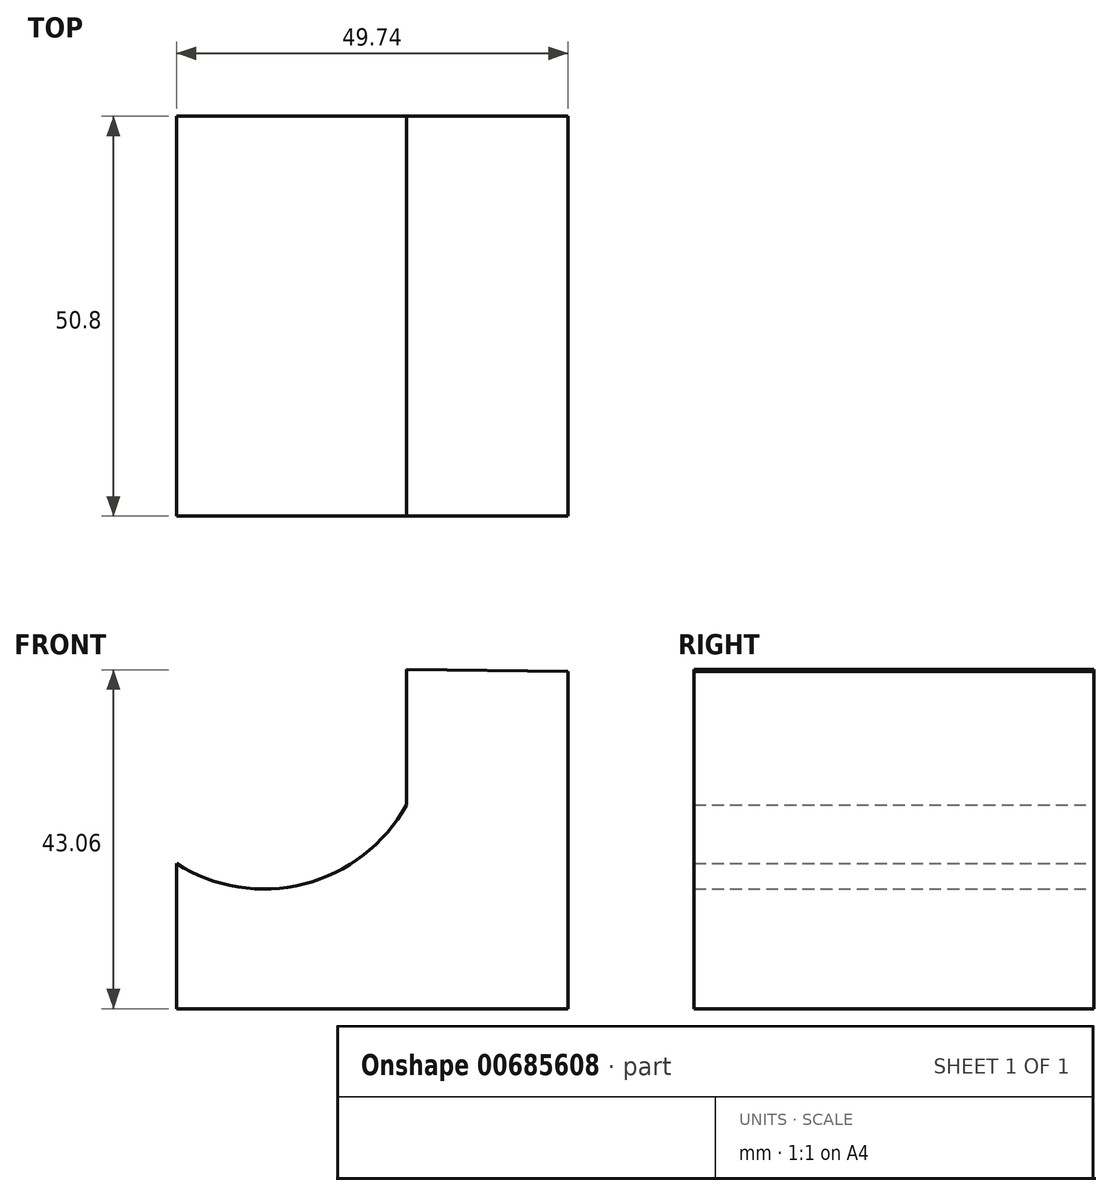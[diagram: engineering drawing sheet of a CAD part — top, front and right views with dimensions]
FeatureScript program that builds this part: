
annotation { "Feature Type Name" : "Feature", "Feature Type Description" : "" }
export const myFeature = defineFeature(function(context is Context, id is Id, definition is map)
    precondition{}
    {
        {
            var Q0;
            Q0=qCreatedBy(makeId("Front.planeOp"),FACE);
            var sketch = newSketch(context, id + "F0", { "sketchPlane" : qUnion([Q0])});
            skLineSegment(sketch, "E0", {"start": v(0, 42.87) * mm, "end": v(0, 0) * mm});
            skLineSegment(sketch, "E1", {"start": v(0, 0) * mm, "end": v(-49.74, 0) * mm});
            skLineSegment(sketch, "E2", {"start": v(-49.74, 0) * mm, "end": v(-49.74, 18.43) * mm});
            skArc(sketch, "E3", {"start": v(-49.74, 18.43) * mm, "mid": v(-33.52, 15.83) * mm, "end": v(-20.53, 25.87) * mm});
            skLineSegment(sketch, "E4", {"start": v(-20.53, 25.87) * mm, "end": v(-20.53, 43.06) * mm});
            skLineSegment(sketch, "E5", {"start": v(-20.53, 43.06) * mm, "end": v(0, 42.87) * mm});
            skSolve(sketch);
        }
        {
            var Q0;
            Q0 = qSketchRegion(id + "F0", true);
            extrude(context, id + "F1", {"entities" : qUnion([Q0]), "depth" : 50.8 * mm, "offsetDistance" : 25.4 * mm});
        }
    });
